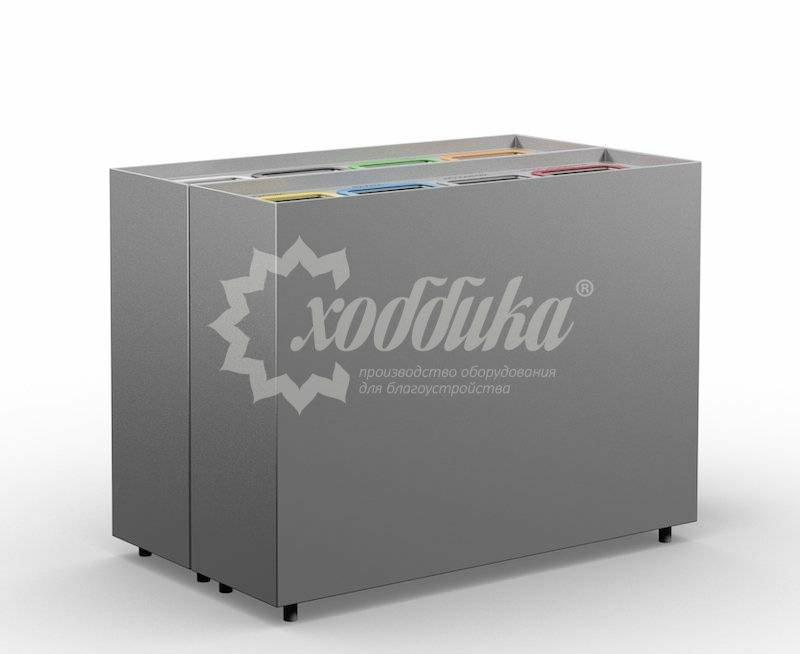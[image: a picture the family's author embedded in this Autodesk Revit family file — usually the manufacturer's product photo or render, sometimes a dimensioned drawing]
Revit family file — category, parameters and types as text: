
# Revit family: Урна для раздельного сбора мусора «Серво» Арт 12773
name_source: partatom
category: Антураж
revit_build: Autodesk Revit 2018 (Build: 20180423_1000(x64)
units: mm (PartAtom-declared; Revit-internal decimal feet)

## family parameters
Всегда вертикально = Да
Источник визуального образа = Геометрия семейства
На основе рабочей плоскости = Нет
Общий = Нет
При загрузке вырезать с полостями = Нет
Точка расчета площади = Нет

## types (2) — shared parameters
URL = https://hobbyka.ru
Артикул товара = Арт. 12773
Высота = 780 мм
Группа модели = Уличные урны
Длина = 1200 мм
Изготовитель = ООО «Хоббика»
Материал изделия = Сталь
Цвет урны = Сталь
Цвет урны для батареек = Для батареек
Ширина = 300 мм

## per-type parameters (varying)
| type | Изображение типоразмера | Описание | Урна для батареек |
| 4 секции плюс урна для батареек | Урна для раздельного сбора мусора «Серво» 4 секции плюс урна для батареек Арт 12773.jpg | Урна для раздельного сбора мусора «Серво». 4 секции плюс урна для батареек | Да |
| 4 секции | Урна для раздельного сбора мусора «Серво» 4 секции Арт 12773.jpg | Урна для раздельного сбора мусора «Серво». 4 секции | Нет |
